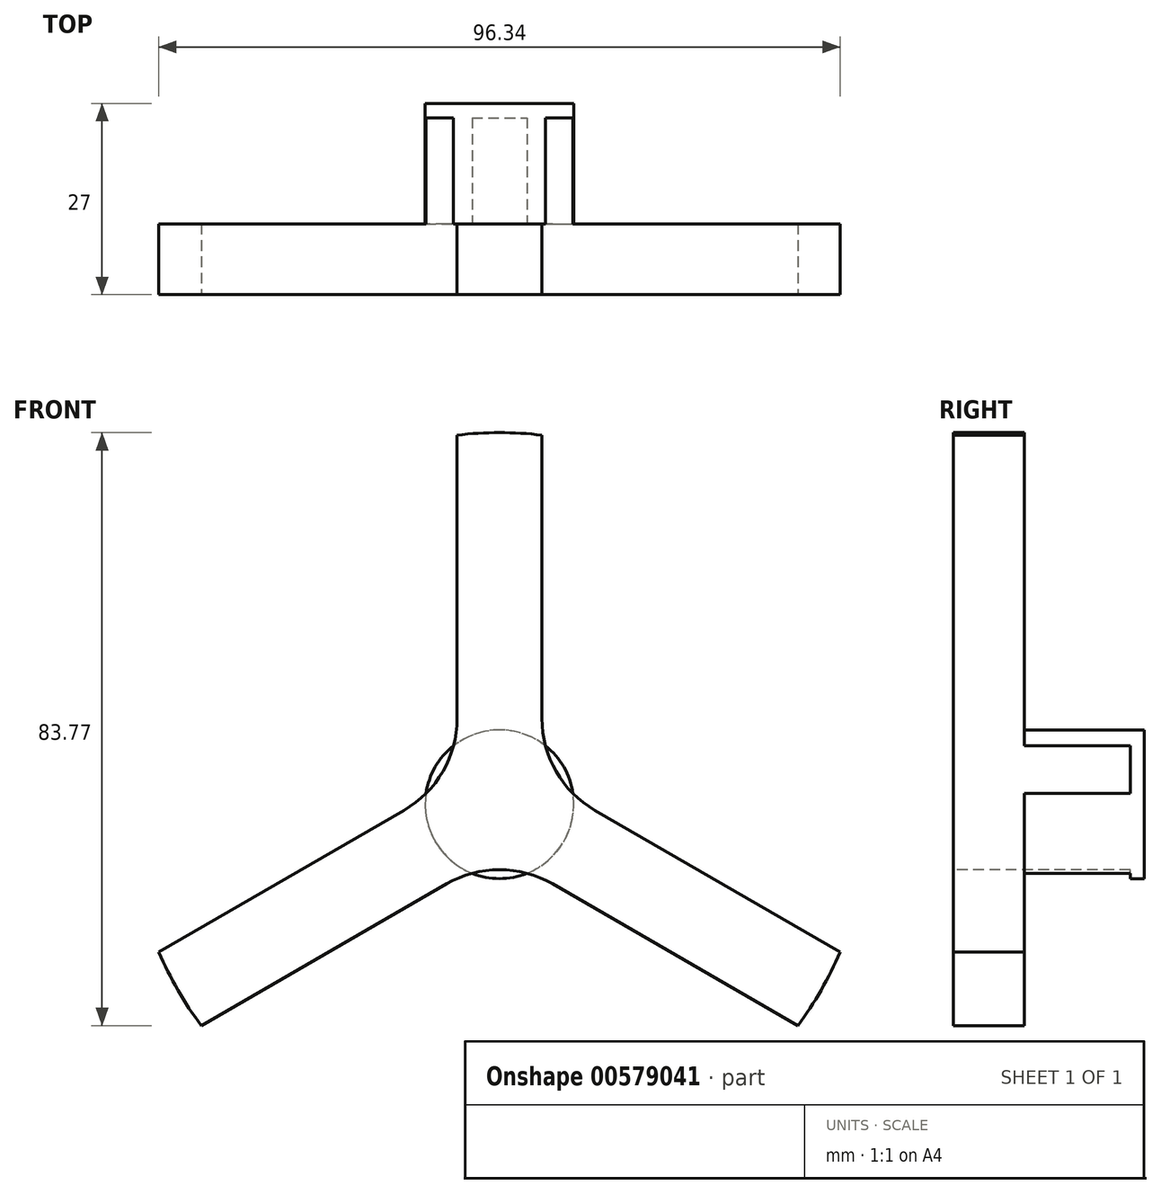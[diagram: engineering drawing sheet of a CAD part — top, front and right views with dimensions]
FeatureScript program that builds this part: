
annotation { "Feature Type Name" : "Feature", "Feature Type Description" : "" }
export const myFeature = defineFeature(function(context is Context, id is Id, definition is map)
    precondition{}
    {
        {
            var Q0;
            Q0=qCreatedBy(makeId("Front.planeOp"),FACE);
            var sketch = newSketch(context, id + "F0", { "sketchPlane" : qUnion([Q0])});
            skCircle(sketch, "E0", {"center": v(0, 0) * mm, "radius": 10.5 * mm});
            skSolve(sketch);
        }
        {
            var Q0;
            Q0=makeQuery(id+"F0.imprint","IMPRINT",FACE,{"disambiguationData":[TD([[makeQuery(id+"F0.imprint","IMPRINT",EDGE,{"derivedFrom":sQuery(id+"F0.wireOp",EDGE,"E0")}),1.0]])]});
            extrude(context, id + "F1", {"entities" : qUnion([Q0]), "depth" : 17 * mm, "offsetDistance" : 25 * mm});
        }
        {
            var Q0;
            Q0=makeQuery(id+"F1.opExtrude","CAP_FACE",FACE,{"disambiguationData":[OSD([sQuery(id+"F0.wireOp",EDGE,"E0")])],"isStart":false});
            var sketch = newSketch(context, id + "F2", { "sketchPlane" : qUnion([Q0])});
            skCircle(sketch, "E1", {"center": v(0, 0) * mm, "radius": 52.5 * mm});
            skSolve(sketch);
        }
        {
            var Q0;
            Q0 = qSketchRegion(id + "F2", true);
            extrude(context, id + "F3", {"entities" : qUnion([Q0]), "operationType" : NewBodyOperationType.ADD, "depth" : 10 * mm, "offsetDistance" : 25 * mm});
        }
        {
            var Q0;
            Q0=makeQuery(id+"F3.opExtrude","CAP_FACE",FACE,{"disambiguationData":[OSD([sQuery(id+"F2.wireOp",EDGE,"E1")])],"isStart":false});
            var sketch = newSketch(context, id + "F4", { "sketchPlane" : qUnion([Q0])});
            skLineSegment(sketch, "E2", {"start": v(-6, 12.12) * mm, "end": v(-6, 52.16) * mm});
            skLineSegment(sketch, "E3", {"start": v(6, 12.12) * mm, "end": v(6, 52.16) * mm});
            skLineSegment(sketch, "E4.1.0", {"start": v(-7.5, -11.26) * mm, "end": v(-42.17, -31.27) * mm});
            skLineSegment(sketch, "E4.1.1", {"start": v(-13.5, -0.87) * mm, "end": v(-48.17, -20.88) * mm});
            skLineSegment(sketch, "E4.2.0", {"start": v(13.5, -0.87) * mm, "end": v(48.17, -20.88) * mm});
            skLineSegment(sketch, "E4.2.1", {"start": v(7.5, -11.26) * mm, "end": v(42.17, -31.27) * mm});
            skPoint(sketch, "E4.center", {"position": v(0, 0) * mm});
            skArc(sketch, "E5", {"start": v(-48.17, -20.88) * mm, "mid": v(-45.47, -26.25) * mm, "end": v(-42.17, -31.27) * mm});
            skArc(sketch, "E6.trimOffspring", {"start": v(6, 52.16) * mm, "mid": v(0, 52.5) * mm, "end": v(-6, 52.16) * mm});
            skArc(sketch, "E7.trimOffspring", {"start": v(42.17, -31.27) * mm, "mid": v(45.47, -26.25) * mm, "end": v(48.17, -20.88) * mm});
            skPoint(sketch, "E8.visualSharp", {"position": v(6, 3.46) * mm});
            skArc(sketch, "E8.filletArc", {"start": v(6, 12.12) * mm, "mid": v(8, 4.62) * mm, "end": v(13.5, -0.87) * mm});
            skPoint(sketch, "E9.visualSharp", {"position": v(-6, 3.46) * mm});
            skArc(sketch, "E9.filletArc", {"start": v(-13.5, -0.87) * mm, "mid": v(-8, 4.62) * mm, "end": v(-6, 12.12) * mm});
            skPoint(sketch, "E10.visualSharp", {"position": v(0, -6.93) * mm});
            skArc(sketch, "E10.filletArc", {"start": v(7.5, -11.26) * mm, "mid": v(0, -9.25) * mm, "end": v(-7.5, -11.26) * mm});
            skLineSegment(sketch, "E11", {"start": v(6, 52.16) * mm, "end": v(6, 64.16) * mm});
            skLineSegment(sketch, "E12", {"start": v(48.17, -20.88) * mm, "end": v(58.56, -26.88) * mm});
            skSolve(sketch);
        }
        {
            var Q0;
            {var subQ0=sQuery(id+"F4.wireOp",EDGE,"E2");Q0=makeQuery(id+"F4.imprint","IMPRINT",FACE,{"disambiguationData":[TD([[makeQuery(id+"F4.imprint","IMPRINT",EDGE,{"derivedFrom":subQ0}),1.0]])]});}
            var Q1;
            {var subQ0=sQuery(id+"F4.wireOp",EDGE,"E3");Q1=makeQuery(id+"F4.imprint","IMPRINT",FACE,{"disambiguationData":[TD([[makeQuery(id+"F4.imprint","IMPRINT",EDGE,{"derivedFrom":subQ0}),-1.0]])]});}
            var Q2;
            {var subQ0=sQuery(id+"F4.wireOp",EDGE,"E4.1.0");Q2=makeQuery(id+"F4.imprint","IMPRINT",FACE,{"disambiguationData":[TD([[makeQuery(id+"F4.imprint","IMPRINT",EDGE,{"derivedFrom":subQ0}),1.0]])]});}
            extrude(context, id + "F5", {"entities" : qUnion([Q0, Q1, Q2]), "operationType" : NewBodyOperationType.REMOVE, "oppositeDirection" : true, "depth" : 25 * mm, "offsetDistance" : 25 * mm});
        }
    });
